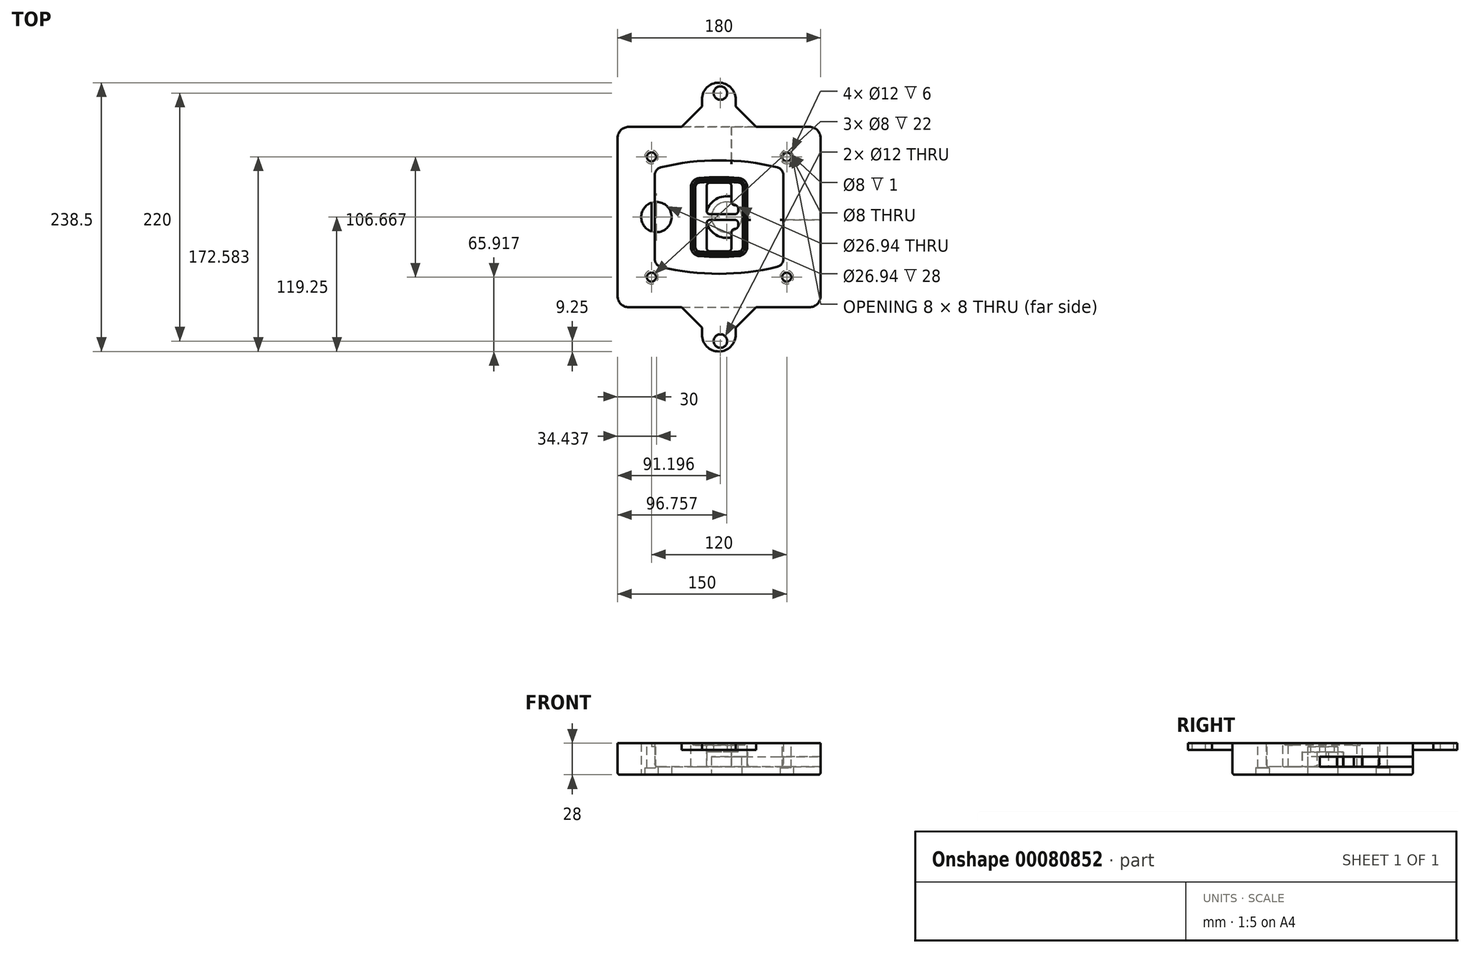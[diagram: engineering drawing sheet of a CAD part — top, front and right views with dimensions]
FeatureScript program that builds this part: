
annotation { "Feature Type Name" : "Feature", "Feature Type Description" : "" }
export const myFeature = defineFeature(function(context is Context, id is Id, definition is map)
    precondition{}
    {
        {
            var Q0;
            Q0=qCreatedBy(makeId("Top.planeOp"),FACE);
            var sketch = newSketch(context, id + "F0", { "sketchPlane" : qUnion([Q0])});
            skPoint(sketch, "E0.rect.middle", {"position": v(0, 0) * mm});
            skLineSegment(sketch, "E1.bottom", {"start": v(-80, -80) * mm, "end": v(80, -80) * mm});
            skLineSegment(sketch, "E1.top", {"start": v(-80, 80) * mm, "end": v(80, 80) * mm});
            skLineSegment(sketch, "E1.left", {"start": v(-90, -70) * mm, "end": v(-90, 70) * mm});
            skLineSegment(sketch, "E1.right", {"start": v(90, -70) * mm, "end": v(90, 70) * mm});
            skLineSegment(sketch, "E2", {"start": v(-90, 80) * mm, "end": v(90, -80) * mm, "construction": true});
            skLineSegment(sketch, "E3", {"start": v(90, 80) * mm, "end": v(-90, -80) * mm, "construction": true});
            skCircle(sketch, "E4", {"center": v(-60, 53.33) * mm, "radius": 4 * mm});
            skCircle(sketch, "E5", {"center": v(60, 53.33) * mm, "radius": 4 * mm});
            skCircle(sketch, "E6", {"center": v(60, -53.33) * mm, "radius": 4 * mm});
            skCircle(sketch, "E7", {"center": v(-60, -53.33) * mm, "radius": 4 * mm});
            skLineSegment(sketch, "E8", {"start": v(-60, 53.33) * mm, "end": v(60, 53.33) * mm, "construction": true});
            skLineSegment(sketch, "E9", {"start": v(60, 53.33) * mm, "end": v(60, -53.33) * mm, "construction": true});
            skLineSegment(sketch, "E10", {"start": v(60, -53.33) * mm, "end": v(-60, -53.33) * mm, "construction": true});
            skLineSegment(sketch, "E11", {"start": v(-60, -53.33) * mm, "end": v(-60, 53.33) * mm, "construction": true});
            skLineSegment(sketch, "E12", {"start": v(-60, 37.3) * mm, "end": v(-60, -37.3) * mm});
            skLineSegment(sketch, "E13", {"start": v(60, 37.3) * mm, "end": v(60, -37.3) * mm});
            skArc(sketch, "E14", {"start": v(52.38, 47.01) * mm, "mid": v(0, 53.33) * mm, "end": v(-52.38, 47.01) * mm});
            skArc(sketch, "E15", {"start": v(-52.38, -47.01) * mm, "mid": v(0, -53.33) * mm, "end": v(52.38, -47.01) * mm});
            skLineSegment(sketch, "E16", {"start": v(-60, 0) * mm, "end": v(60, 0) * mm, "construction": true});
            skPoint(sketch, "E17.visualSharp", {"position": v(-60, -45) * mm});
            skArc(sketch, "E17.filletArc", {"start": v(-60, -37.3) * mm, "mid": v(-57.87, -43.47) * mm, "end": v(-52.38, -47.01) * mm});
            skPoint(sketch, "E18.visualSharp", {"position": v(-60, 45) * mm});
            skArc(sketch, "E18.filletArc", {"start": v(-52.38, 47.01) * mm, "mid": v(-57.87, 43.47) * mm, "end": v(-60, 37.3) * mm});
            skPoint(sketch, "E19.visualSharp", {"position": v(60, 45) * mm});
            skArc(sketch, "E19.filletArc", {"start": v(60, 37.3) * mm, "mid": v(57.87, 43.47) * mm, "end": v(52.38, 47.01) * mm});
            skPoint(sketch, "E20.visualSharp", {"position": v(60, -45) * mm});
            skArc(sketch, "E20.filletArc", {"start": v(52.38, -47.01) * mm, "mid": v(57.87, -43.47) * mm, "end": v(60, -37.3) * mm});
            skPoint(sketch, "E21.visualSharp", {"position": v(-90, 80) * mm});
            skArc(sketch, "E21.filletArc", {"start": v(-80, 80) * mm, "mid": v(-87.07, 77.07) * mm, "end": v(-90, 70) * mm});
            skPoint(sketch, "E22.visualSharp", {"position": v(90, 80) * mm});
            skArc(sketch, "E22.filletArc", {"start": v(90, 70) * mm, "mid": v(87.07, 77.07) * mm, "end": v(80, 80) * mm});
            skPoint(sketch, "E23.visualSharp", {"position": v(90, -80) * mm});
            skArc(sketch, "E23.filletArc", {"start": v(80, -80) * mm, "mid": v(87.07, -77.07) * mm, "end": v(90, -70) * mm});
            skPoint(sketch, "E24.visualSharp", {"position": v(-90, -80) * mm});
            skArc(sketch, "E24.filletArc", {"start": v(-90, -70) * mm, "mid": v(-87.07, -77.07) * mm, "end": v(-80, -80) * mm});
            skArc(sketch, "E25.0", {"start": v(57, 37.3) * mm, "mid": v(55.5, 41.62) * mm, "end": v(51.67, 44.1) * mm});
            skLineSegment(sketch, "E25.1", {"start": v(57, 37.3) * mm, "end": v(57, -37.3) * mm});
            skArc(sketch, "E25.2", {"start": v(51.67, -44.1) * mm, "mid": v(55.5, -41.62) * mm, "end": v(57, -37.3) * mm});
            skArc(sketch, "E25.3", {"start": v(-51.67, -44.1) * mm, "mid": v(0, -50.33) * mm, "end": v(51.67, -44.1) * mm});
            skArc(sketch, "E25.4", {"start": v(-57, -37.3) * mm, "mid": v(-55.5, -41.62) * mm, "end": v(-51.67, -44.1) * mm});
            skArc(sketch, "E25.5", {"start": v(51.67, 44.1) * mm, "mid": v(0, 50.33) * mm, "end": v(-51.67, 44.1) * mm});
            skLineSegment(sketch, "E25.6", {"start": v(-57, 37.3) * mm, "end": v(-57, -37.3) * mm});
            skArc(sketch, "E25.7", {"start": v(-51.67, 44.1) * mm, "mid": v(-55.5, 41.62) * mm, "end": v(-57, 37.3) * mm});
            skArc(sketch, "E26.0", {"start": v(-53.33, 50.9) * mm, "mid": v(-61.01, 45.94) * mm, "end": v(-64, 37.3) * mm});
            skArc(sketch, "E26.1", {"start": v(53.33, 50.9) * mm, "mid": v(0, 57.33) * mm, "end": v(-53.33, 50.9) * mm});
            skArc(sketch, "E26.2", {"start": v(64, 37.3) * mm, "mid": v(61.01, 45.94) * mm, "end": v(53.33, 50.9) * mm});
            skLineSegment(sketch, "E26.3", {"start": v(64, 37.3) * mm, "end": v(64, -37.3) * mm});
            skArc(sketch, "E26.4", {"start": v(53.33, -50.9) * mm, "mid": v(61.01, -45.94) * mm, "end": v(64, -37.3) * mm});
            skLineSegment(sketch, "E26.5", {"start": v(-64, 37.3) * mm, "end": v(-64, -37.3) * mm});
            skArc(sketch, "E26.6", {"start": v(-53.33, -50.9) * mm, "mid": v(0, -57.33) * mm, "end": v(53.33, -50.9) * mm});
            skArc(sketch, "E26.7", {"start": v(-64, -37.3) * mm, "mid": v(-61.01, -45.94) * mm, "end": v(-53.33, -50.9) * mm});
            skSolve(sketch);
        }
        {
            var Q0;
            Q0=makeQuery(id+"F0.imprint","IMPRINT",FACE,{"disambiguationData":[TD([[makeQuery(id+"F0.imprint","IMPRINT",EDGE,{"derivedFrom":sQuery(id+"F0.wireOp",EDGE,"E1.bottom")}),1.0]])]});
            var Q1;
            Q1=makeQuery(id+"F0.imprint","IMPRINT",FACE,{"disambiguationData":[TD([[makeQuery(id+"F0.imprint","IMPRINT",EDGE,{"derivedFrom":sQuery(id+"F0.wireOp",EDGE,"E12")}),1.0]])]});
            var Q2;
            Q2=makeQuery(id+"F0.imprint","IMPRINT",FACE,{"disambiguationData":[TD([[makeQuery(id+"F0.imprint","IMPRINT",EDGE,{"derivedFrom":sQuery(id+"F0.wireOp",EDGE,"E25.0")}),1.0]])]});
            var Q3;
            Q3=makeQuery(id+"F0.imprint","IMPRINT",FACE,{"disambiguationData":[TD([[makeQuery(id+"F0.imprint","IMPRINT",EDGE,{"derivedFrom":sQuery(id+"F0.wireOp",EDGE,"E12")}),-1.0]])]});
            extrude(context, id + "F1", {"entities" : qUnion([Q0, Q1, Q2, Q3]), "oppositeDirection" : true, "depth" : 25 * mm});
        }
        {
            var Q0;
            Q0=makeQuery(id+"F0.imprint","IMPRINT",FACE,{"disambiguationData":[TD([[makeQuery(id+"F0.imprint","IMPRINT",EDGE,{"derivedFrom":sQuery(id+"F0.wireOp",EDGE,"E12")}),1.0]])]});
            extrude(context, id + "F2", {"entities" : qUnion([Q0]), "operationType" : NewBodyOperationType.ADD, "depth" : 3 * mm});
        }
        {
            var Q0;
            Q0=makeQuery(id+"F0.imprint","IMPRINT",FACE,{"disambiguationData":[TD([[makeQuery(id+"F0.imprint","IMPRINT",EDGE,{"derivedFrom":sQuery(id+"F0.wireOp",EDGE,"E25.0")}),1.0]])]});
            extrude(context, id + "F3", {"entities" : qUnion([Q0]), "operationType" : NewBodyOperationType.REMOVE, "oppositeDirection" : true, "depth" : 18 * mm});
        }
        {
            var Q0;
            Q0=makeQuery(id+"F2.opExtrude","CAP_FACE",FACE,{"disambiguationData":[OSD([sQuery(id+"F0.wireOp",EDGE,"E12"),sQuery(id+"F0.wireOp",EDGE,"E13"),sQuery(id+"F0.wireOp",EDGE,"E14"),sQuery(id+"F0.wireOp",EDGE,"E15"),sQuery(id+"F0.wireOp",EDGE,"E17.filletArc"),sQuery(id+"F0.wireOp",EDGE,"E18.filletArc"),sQuery(id+"F0.wireOp",EDGE,"E19.filletArc"),sQuery(id+"F0.wireOp",EDGE,"E20.filletArc"),sQuery(id+"F0.wireOp",EDGE,"E25.0"),sQuery(id+"F0.wireOp",EDGE,"E25.1"),sQuery(id+"F0.wireOp",EDGE,"E25.2"),sQuery(id+"F0.wireOp",EDGE,"E25.3"),sQuery(id+"F0.wireOp",EDGE,"E25.4"),sQuery(id+"F0.wireOp",EDGE,"E25.5"),sQuery(id+"F0.wireOp",EDGE,"E25.6"),sQuery(id+"F0.wireOp",EDGE,"E25.7")])],"isStart":false});
            var sketch = newSketch(context, id + "F4", { "sketchPlane" : qUnion([Q0])});
            skArc(sketch, "E27.0", {"start": v(-17.7, -34.56) * mm, "mid": v(0, -35.33) * mm, "end": v(17.7, -34.56) * mm});
            skArc(sketch, "E28.0", {"start": v(17.7, 34.56) * mm, "mid": v(0, 35.33) * mm, "end": v(-17.7, 34.56) * mm});
            skLineSegment(sketch, "E29", {"start": v(-25, 26.59) * mm, "end": v(-25, -26.59) * mm});
            skLineSegment(sketch, "E30", {"start": v(25, 26.59) * mm, "end": v(25, -26.59) * mm});
            skLineSegment(sketch, "E31", {"start": v(-25, 33.78) * mm, "end": v(25, 33.78) * mm, "construction": true});
            skLineSegment(sketch, "E32", {"start": v(-25, -33.78) * mm, "end": v(25, -33.78) * mm, "construction": true});
            skPoint(sketch, "E33.visualSharp", {"position": v(-25, 33.78) * mm});
            skArc(sketch, "E33.filletArc", {"start": v(-17.7, 34.56) * mm, "mid": v(-22.9, 32) * mm, "end": v(-25, 26.59) * mm});
            skPoint(sketch, "E34.visualSharp", {"position": v(25, 33.78) * mm});
            skArc(sketch, "E34.filletArc", {"start": v(25, 26.59) * mm, "mid": v(22.9, 32) * mm, "end": v(17.7, 34.56) * mm});
            skPoint(sketch, "E35.visualSharp", {"position": v(25, -33.78) * mm});
            skArc(sketch, "E35.filletArc", {"start": v(17.7, -34.56) * mm, "mid": v(22.9, -32) * mm, "end": v(25, -26.59) * mm});
            skPoint(sketch, "E36.visualSharp", {"position": v(-25, -33.78) * mm});
            skArc(sketch, "E36.filletArc", {"start": v(-25, -26.59) * mm, "mid": v(-22.9, -32) * mm, "end": v(-17.7, -34.56) * mm});
            skArc(sketch, "E37.0", {"start": v(51.67, 44.1) * mm, "mid": v(0, 50.33) * mm, "end": v(-51.67, 44.1) * mm});
            skArc(sketch, "E37.1", {"start": v(-51.67, 44.1) * mm, "mid": v(-55.5, 41.62) * mm, "end": v(-57, 37.3) * mm});
            skLineSegment(sketch, "E37.2", {"start": v(-57, 37.3) * mm, "end": v(-57, -37.3) * mm});
            skArc(sketch, "E37.3", {"start": v(-57, -37.3) * mm, "mid": v(-55.5, -41.62) * mm, "end": v(-51.67, -44.1) * mm});
            skArc(sketch, "E37.4", {"start": v(-51.67, -44.1) * mm, "mid": v(0, -50.33) * mm, "end": v(51.67, -44.1) * mm});
            skArc(sketch, "E37.5", {"start": v(51.67, -44.1) * mm, "mid": v(55.5, -41.62) * mm, "end": v(57, -37.3) * mm});
            skLineSegment(sketch, "E37.6", {"start": v(57, 37.3) * mm, "end": v(57, -37.3) * mm});
            skArc(sketch, "E37.7", {"start": v(57, 37.3) * mm, "mid": v(55.5, 41.62) * mm, "end": v(51.67, 44.1) * mm});
            skLineSegment(sketch, "E38.0", {"start": v(23, 26.59) * mm, "end": v(23, -26.59) * mm});
            skArc(sketch, "E38.1", {"start": v(17.53, -32.56) * mm, "mid": v(21.42, -30.64) * mm, "end": v(23, -26.59) * mm});
            skArc(sketch, "E38.2", {"start": v(-17.53, -32.56) * mm, "mid": v(0, -33.33) * mm, "end": v(17.53, -32.56) * mm});
            skArc(sketch, "E38.3", {"start": v(-23, -26.59) * mm, "mid": v(-21.42, -30.64) * mm, "end": v(-17.53, -32.56) * mm});
            skLineSegment(sketch, "E38.4", {"start": v(-23, 26.59) * mm, "end": v(-23, -26.59) * mm});
            skArc(sketch, "E38.5", {"start": v(23, 26.59) * mm, "mid": v(21.42, 30.64) * mm, "end": v(17.53, 32.56) * mm});
            skArc(sketch, "E38.6", {"start": v(-17.53, 32.56) * mm, "mid": v(-21.42, 30.64) * mm, "end": v(-23, 26.59) * mm});
            skArc(sketch, "E38.7", {"start": v(17.53, 32.56) * mm, "mid": v(0, 33.33) * mm, "end": v(-17.53, 32.56) * mm});
            skArc(sketch, "E39.0", {"start": v(21, 26.59) * mm, "mid": v(19.95, 29.29) * mm, "end": v(17.35, 30.57) * mm});
            skLineSegment(sketch, "E39.1", {"start": v(21, 26.59) * mm, "end": v(21, -26.59) * mm});
            skArc(sketch, "E39.2", {"start": v(17.35, -30.57) * mm, "mid": v(19.95, -29.29) * mm, "end": v(21, -26.59) * mm});
            skArc(sketch, "E39.3", {"start": v(-17.35, -30.57) * mm, "mid": v(0, -31.33) * mm, "end": v(17.35, -30.57) * mm});
            skArc(sketch, "E39.4", {"start": v(-21, -26.59) * mm, "mid": v(-19.95, -29.29) * mm, "end": v(-17.35, -30.57) * mm});
            skArc(sketch, "E39.5", {"start": v(17.35, 30.57) * mm, "mid": v(0, 31.33) * mm, "end": v(-17.35, 30.57) * mm});
            skLineSegment(sketch, "E39.6", {"start": v(-21, 26.59) * mm, "end": v(-21, -26.59) * mm});
            skArc(sketch, "E39.7", {"start": v(-17.35, 30.57) * mm, "mid": v(-19.95, 29.29) * mm, "end": v(-21, 26.59) * mm});
            skLineSegment(sketch, "E40", {"start": v(-25, 0) * mm, "end": v(25, 0) * mm, "construction": true});
            skLineSegment(sketch, "E41", {"start": v(-11, 5.5) * mm, "end": v(-11, 27.5) * mm});
            skLineSegment(sketch, "E42", {"start": v(-8, 30.5) * mm, "end": v(8, 30.5) * mm});
            skLineSegment(sketch, "E43", {"start": v(11, 27.5) * mm, "end": v(11, 13.5) * mm});
            skLineSegment(sketch, "E44", {"start": v(14, 10.5) * mm, "end": v(14, 10.5) * mm});
            skLineSegment(sketch, "E45", {"start": v(17, 7.5) * mm, "end": v(17, 5.5) * mm});
            skLineSegment(sketch, "E46", {"start": v(14, 2.5) * mm, "end": v(-8, 2.5) * mm});
            skPoint(sketch, "E47.visualSharp", {"position": v(-11, 30.5) * mm});
            skArc(sketch, "E47.filletArc", {"start": v(-8, 30.5) * mm, "mid": v(-10.12, 29.62) * mm, "end": v(-11, 27.5) * mm});
            skPoint(sketch, "E48.visualSharp", {"position": v(11, 30.5) * mm});
            skArc(sketch, "E48.filletArc", {"start": v(11, 27.5) * mm, "mid": v(10.12, 29.62) * mm, "end": v(8, 30.5) * mm});
            skPoint(sketch, "E49.visualSharp", {"position": v(11, 10.5) * mm});
            skArc(sketch, "E49.filletArc", {"start": v(11, 13.5) * mm, "mid": v(11.88, 11.38) * mm, "end": v(14, 10.5) * mm});
            skPoint(sketch, "E50.visualSharp", {"position": v(17, 10.5) * mm});
            skArc(sketch, "E50.filletArc", {"start": v(17, 7.5) * mm, "mid": v(16.12, 9.62) * mm, "end": v(14, 10.5) * mm});
            skPoint(sketch, "E51.visualSharp", {"position": v(17, 2.5) * mm});
            skArc(sketch, "E51.filletArc", {"start": v(14, 2.5) * mm, "mid": v(16.12, 3.38) * mm, "end": v(17, 5.5) * mm});
            skPoint(sketch, "E52.visualSharp", {"position": v(-11, 2.5) * mm});
            skArc(sketch, "E52.filletArc", {"start": v(-11, 5.5) * mm, "mid": v(-10.12, 3.38) * mm, "end": v(-8, 2.5) * mm});
            skLineSegment(sketch, "E53.0.MirrorCS", {"start": v(14, -2.5) * mm, "end": v(-8, -2.5) * mm});
            skArc(sketch, "E54.0.MirrorCS", {"start": v(-11, -5.5) * mm, "mid": v(-10.12, -3.38) * mm, "end": v(-8, -2.5) * mm});
            skLineSegment(sketch, "E55.0.MirrorCS", {"start": v(-11, -5.5) * mm, "end": v(-11, -27.5) * mm});
            skArc(sketch, "E56.0.MirrorCS", {"start": v(-8, -30.5) * mm, "mid": v(-10.12, -29.62) * mm, "end": v(-11, -27.5) * mm});
            skLineSegment(sketch, "E57.0.MirrorCS", {"start": v(-8, -30.5) * mm, "end": v(8, -30.5) * mm});
            skArc(sketch, "E58.0.MirrorCS", {"start": v(11, -27.5) * mm, "mid": v(10.12, -29.62) * mm, "end": v(8, -30.5) * mm});
            skLineSegment(sketch, "E59.0.MirrorCS", {"start": v(11, -27.5) * mm, "end": v(11, -13.5) * mm});
            skArc(sketch, "E60.0.MirrorCS", {"start": v(11, -13.5) * mm, "mid": v(11.88, -11.38) * mm, "end": v(14, -10.5) * mm});
            skArc(sketch, "E61.0.MirrorCS", {"start": v(17, -7.5) * mm, "mid": v(16.12, -9.62) * mm, "end": v(14, -10.5) * mm});
            skLineSegment(sketch, "E62.0.MirrorCS", {"start": v(17, -7.5) * mm, "end": v(17, -5.5) * mm});
            skArc(sketch, "E63.0.MirrorCS", {"start": v(14, -2.5) * mm, "mid": v(16.12, -3.38) * mm, "end": v(17, -5.5) * mm});
            skSolve(sketch);
        }
        {
            var Q0;
            Q0=makeQuery(id+"F4.imprint","IMPRINT",FACE,{"disambiguationData":[TD([[makeQuery(id+"F4.imprint","IMPRINT",EDGE,{"derivedFrom":sQuery(id+"F4.wireOp",EDGE,"E27.0")}),1.0]])]});
            var Q1;
            Q1=makeQuery(id+"F4.imprint","IMPRINT",FACE,{"disambiguationData":[TD([[makeQuery(id+"F4.imprint","IMPRINT",EDGE,{"derivedFrom":sQuery(id+"F4.wireOp",EDGE,"E38.0")}),-1.0]])]});
            var Q2;
            Q2=makeQuery(id+"F4.imprint","IMPRINT",FACE,{"disambiguationData":[TD([[makeQuery(id+"F4.imprint","IMPRINT",EDGE,{"derivedFrom":sQuery(id+"F4.wireOp",EDGE,"E39.0")}),1.0]])]});
            extrude(context, id + "F5", {"entities" : qUnion([Q0, Q1, Q2]), "operationType" : NewBodyOperationType.ADD, "endBound" : BoundingType.UP_TO_NEXT, "oppositeDirection" : true, "depth" : 25 * mm});
        }
        {
            var Q0;
            Q0=makeQuery(id+"F4.imprint","IMPRINT",FACE,{"disambiguationData":[TD([[makeQuery(id+"F4.imprint","IMPRINT",EDGE,{"derivedFrom":sQuery(id+"F4.wireOp",EDGE,"E38.0")}),-1.0]])]});
            extrude(context, id + "F6", {"entities" : qUnion([Q0]), "operationType" : NewBodyOperationType.REMOVE, "oppositeDirection" : true, "depth" : 2 * mm});
        }
        {
            var Q0;
            Q0=makeQuery(id+"F1.opExtrude","CAP_FACE",FACE,{"disambiguationData":[OSD([sQuery(id+"F0.wireOp",EDGE,"E1.bottom"),sQuery(id+"F0.wireOp",EDGE,"E1.top"),sQuery(id+"F0.wireOp",EDGE,"E1.left"),sQuery(id+"F0.wireOp",EDGE,"E1.right"),sQuery(id+"F0.wireOp",EDGE,"E4"),sQuery(id+"F0.wireOp",EDGE,"E5"),sQuery(id+"F0.wireOp",EDGE,"E6"),sQuery(id+"F0.wireOp",EDGE,"E7"),sQuery(id+"F0.wireOp",EDGE,"E21.filletArc"),sQuery(id+"F0.wireOp",EDGE,"E22.filletArc"),sQuery(id+"F0.wireOp",EDGE,"E23.filletArc"),sQuery(id+"F0.wireOp",EDGE,"E24.filletArc")])],"isStart":false});
            var sketch = newSketch(context, id + "F7", { "sketchPlane" : qUnion([Q0])});
            skCircle(sketch, "E64", {"center": v(6.76, 0) * mm, "radius": 13.47 * mm});
            skCircle(sketch, "E65", {"center": v(-55.56, 0) * mm, "radius": 13.47 * mm});
            skLineSegment(sketch, "E66", {"start": v(90, 0) * mm, "end": v(-90, 0) * mm});
            skCircle(sketch, "E67", {"center": v(6.76, 0) * mm, "radius": 18.47 * mm});
            skCircle(sketch, "E68", {"center": v(60, -53.33) * mm, "radius": 6 * mm});
            skCircle(sketch, "E69", {"center": v(-60, -53.33) * mm, "radius": 6 * mm});
            skCircle(sketch, "E70", {"center": v(-60, 53.33) * mm, "radius": 6 * mm});
            skCircle(sketch, "E71", {"center": v(60, 53.33) * mm, "radius": 6 * mm});
            skSolve(sketch);
        }
        {
            var Q0;
            {var subQ1=sQuery(id+"F7.wireOp",EDGE,"E66");var subQ4=sQuery(id+"F7.wireOp",EDGE,"E64");var subQ6=makeQuery(id+"F7.imprint","INTERSECT",VERTEX,{"disambiguationData":[OD(0.0)],"derivedFrom":[subQ4,subQ1]});Q0=makeQuery(id+"F7.imprint","IMPRINT",FACE,{"disambiguationData":[TD([[makeQuery(id+"F7.imprint","IMPRINT",EDGE,{"disambiguationData":[TD([[subQ6,-1.0]])],"derivedFrom":subQ4}),-1.0]])]});}
            var Q1;
            {var subQ0=sQuery(id+"F7.wireOp",EDGE,"E66");var subQ1=sQuery(id+"F7.wireOp",EDGE,"E64");var subQ3=makeQuery(id+"F7.imprint","INTERSECT",VERTEX,{"disambiguationData":[OD(0.0)],"derivedFrom":[subQ1,subQ0]});Q1=makeQuery(id+"F7.imprint","IMPRINT",FACE,{"disambiguationData":[TD([[makeQuery(id+"F7.imprint","IMPRINT",EDGE,{"disambiguationData":[TD([[subQ3,-1.0]])],"derivedFrom":subQ1}),1.0]])]});}
            var Q2;
            {var subQ0=sQuery(id+"F7.wireOp",EDGE,"E66");var subQ1=sQuery(id+"F7.wireOp",EDGE,"E64");var subQ3=makeQuery(id+"F7.imprint","INTERSECT",VERTEX,{"disambiguationData":[OD(0.0)],"derivedFrom":[subQ1,subQ0]});Q2=makeQuery(id+"F7.imprint","IMPRINT",FACE,{"disambiguationData":[TD([[makeQuery(id+"F7.imprint","IMPRINT",EDGE,{"disambiguationData":[TD([[subQ3,1.0]])],"derivedFrom":subQ1}),1.0]])]});}
            var Q3;
            {var subQ1=sQuery(id+"F7.wireOp",EDGE,"E66");var subQ4=sQuery(id+"F7.wireOp",EDGE,"E64");var subQ6=makeQuery(id+"F7.imprint","INTERSECT",VERTEX,{"disambiguationData":[OD(0.0)],"derivedFrom":[subQ4,subQ1]});Q3=makeQuery(id+"F7.imprint","IMPRINT",FACE,{"disambiguationData":[TD([[makeQuery(id+"F7.imprint","IMPRINT",EDGE,{"disambiguationData":[TD([[subQ6,1.0]])],"derivedFrom":subQ4}),-1.0]])]});}
            extrude(context, id + "F8", {"entities" : qUnion([Q0, Q1, Q2, Q3]), "operationType" : NewBodyOperationType.ADD, "oppositeDirection" : true, "depth" : 20 * mm});
        }
        {
            var Q0;
            {var subQ0=sQuery(id+"F7.wireOp",EDGE,"E66");var subQ1=sQuery(id+"F7.wireOp",EDGE,"E64");var subQ3=makeQuery(id+"F7.imprint","INTERSECT",VERTEX,{"disambiguationData":[OD(0.0)],"derivedFrom":[subQ1,subQ0]});Q0=makeQuery(id+"F7.imprint","IMPRINT",FACE,{"disambiguationData":[TD([[makeQuery(id+"F7.imprint","IMPRINT",EDGE,{"disambiguationData":[TD([[subQ3,-1.0]])],"derivedFrom":subQ1}),1.0]])]});}
            var Q1;
            {var subQ0=sQuery(id+"F7.wireOp",EDGE,"E66");var subQ1=sQuery(id+"F7.wireOp",EDGE,"E64");var subQ3=makeQuery(id+"F7.imprint","INTERSECT",VERTEX,{"disambiguationData":[OD(0.0)],"derivedFrom":[subQ1,subQ0]});Q1=makeQuery(id+"F7.imprint","IMPRINT",FACE,{"disambiguationData":[TD([[makeQuery(id+"F7.imprint","IMPRINT",EDGE,{"disambiguationData":[TD([[subQ3,1.0]])],"derivedFrom":subQ1}),1.0]])]});}
            extrude(context, id + "F9", {"entities" : qUnion([Q0, Q1]), "operationType" : NewBodyOperationType.REMOVE, "oppositeDirection" : true, "depth" : 16 * mm});
        }
        {
            var Q0;
            {var subQ0=sQuery(id+"F7.wireOp",EDGE,"E66");var subQ1=sQuery(id+"F7.wireOp",EDGE,"E65");var subQ3=makeQuery(id+"F7.imprint","INTERSECT",VERTEX,{"disambiguationData":[OD(0.0)],"derivedFrom":[subQ1,subQ0]});Q0=makeQuery(id+"F7.imprint","IMPRINT",FACE,{"disambiguationData":[TD([[makeQuery(id+"F7.imprint","IMPRINT",EDGE,{"disambiguationData":[TD([[subQ3,-1.0]])],"derivedFrom":subQ1}),1.0]])]});}
            var Q1;
            {var subQ0=sQuery(id+"F7.wireOp",EDGE,"E66");var subQ1=sQuery(id+"F7.wireOp",EDGE,"E65");var subQ3=makeQuery(id+"F7.imprint","INTERSECT",VERTEX,{"disambiguationData":[OD(0.0)],"derivedFrom":[subQ1,subQ0]});Q1=makeQuery(id+"F7.imprint","IMPRINT",FACE,{"disambiguationData":[TD([[makeQuery(id+"F7.imprint","IMPRINT",EDGE,{"disambiguationData":[TD([[subQ3,1.0]])],"derivedFrom":subQ1}),1.0]])]});}
            extrude(context, id + "F10", {"entities" : qUnion([Q0, Q1]), "operationType" : NewBodyOperationType.REMOVE, "oppositeDirection" : true, "depth" : 25 * mm});
        }
        {
            var Q0;
            Q0=makeQuery(id+"F7.imprint","IMPRINT",FACE,{"disambiguationData":[TD([[makeQuery(id+"F7.imprint","IMPRINT",EDGE,{"derivedFrom":sQuery(id+"F7.wireOp",EDGE,"E68")}),1.0]])]});
            var Q1;
            Q1=makeQuery(id+"F7.imprint","IMPRINT",FACE,{"disambiguationData":[TD([[makeQuery(id+"F7.imprint","IMPRINT",EDGE,{"derivedFrom":makeQuery(id+"F1.opExtrude","CAP_EDGE",EDGE,{"disambiguationData":[OSD([sQuery(id+"F0.wireOp",EDGE,"E5")])],"isStart":false})}),-1.0]])]});
            var Q2;
            Q2=makeQuery(id+"F7.imprint","IMPRINT",FACE,{"disambiguationData":[TD([[makeQuery(id+"F7.imprint","IMPRINT",EDGE,{"derivedFrom":sQuery(id+"F7.wireOp",EDGE,"E69")}),1.0]])]});
            var Q3;
            Q3=makeQuery(id+"F7.imprint","IMPRINT",FACE,{"disambiguationData":[TD([[makeQuery(id+"F7.imprint","IMPRINT",EDGE,{"derivedFrom":makeQuery(id+"F1.opExtrude","CAP_EDGE",EDGE,{"disambiguationData":[OSD([sQuery(id+"F0.wireOp",EDGE,"E4")])],"isStart":false})}),-1.0]])]});
            var Q4;
            Q4=makeQuery(id+"F7.imprint","IMPRINT",FACE,{"disambiguationData":[TD([[makeQuery(id+"F7.imprint","IMPRINT",EDGE,{"derivedFrom":sQuery(id+"F7.wireOp",EDGE,"E70")}),1.0]])]});
            var Q5;
            Q5=makeQuery(id+"F7.imprint","IMPRINT",FACE,{"disambiguationData":[TD([[makeQuery(id+"F7.imprint","IMPRINT",EDGE,{"derivedFrom":makeQuery(id+"F1.opExtrude","CAP_EDGE",EDGE,{"disambiguationData":[OSD([sQuery(id+"F0.wireOp",EDGE,"E7")])],"isStart":false})}),-1.0]])]});
            var Q6;
            Q6=makeQuery(id+"F7.imprint","IMPRINT",FACE,{"disambiguationData":[TD([[makeQuery(id+"F7.imprint","IMPRINT",EDGE,{"derivedFrom":sQuery(id+"F7.wireOp",EDGE,"E71")}),1.0]])]});
            var Q7;
            Q7=makeQuery(id+"F7.imprint","IMPRINT",FACE,{"disambiguationData":[TD([[makeQuery(id+"F7.imprint","IMPRINT",EDGE,{"derivedFrom":makeQuery(id+"F1.opExtrude","CAP_EDGE",EDGE,{"disambiguationData":[OSD([sQuery(id+"F0.wireOp",EDGE,"E6")])],"isStart":false})}),-1.0]])]});
            extrude(context, id + "F11", {"entities" : qUnion([Q0, Q1, Q2, Q3, Q4, Q5, Q6, Q7]), "operationType" : NewBodyOperationType.REMOVE, "oppositeDirection" : true, "depth" : 6 * mm});
        }
        {
            var Q0;
            Q0=makeQuery(id+"F9.boolean.opBoolean","COPY",FACE,{"derivedFrom":makeQuery(id+"F9.opExtrude","CAP_FACE",FACE,{"disambiguationData":[OSD([sQuery(id+"F7.wireOp",EDGE,"E64")])],"isStart":false})});
            var sketch = newSketch(context, id + "F12", { "sketchPlane" : qUnion([Q0])});
            skArc(sketch, "E72.0", {"start": v(11, -88.19) * mm, "mid": v(97.1, -83.6) * mm, "end": v(92.5, 2.5) * mm});
            skLineSegment(sketch, "E72.1", {"start": v(11, -17.97) * mm, "end": v(11, -17.97) * mm});
            skLineSegment(sketch, "E73", {"start": v(92.5, -105.13) * mm, "end": v(102.3, -105.13) * mm});
            skLineSegment(sketch, "E74.0", {"start": v(92.5, 2.5) * mm, "end": v(14, 2.5) * mm});
            skArc(sketch, "E74.1", {"start": v(14, 2.5) * mm, "mid": v(16.12, 3.38) * mm, "end": v(17, 5.5) * mm});
            skLineSegment(sketch, "E74.2", {"start": v(17, 7.5) * mm, "end": v(17, 5.5) * mm});
            skArc(sketch, "E74.3", {"start": v(17, 7.5) * mm, "mid": v(16.12, 9.62) * mm, "end": v(14, 10.5) * mm});
            skArc(sketch, "E74.4", {"start": v(11, 13.5) * mm, "mid": v(11.88, 11.38) * mm, "end": v(14, 10.5) * mm});
            skLineSegment(sketch, "E74.5", {"start": v(11, 13.5) * mm, "end": v(11, -88.19) * mm});
            skLineSegment(sketch, "E74.7", {"start": v(92.5, -2.5) * mm, "end": v(14, -2.5) * mm});
            skArc(sketch, "E74.8", {"start": v(14, -2.5) * mm, "mid": v(16.12, -3.38) * mm, "end": v(17, -5.5) * mm});
            skLineSegment(sketch, "E74.9", {"start": v(17, -7.5) * mm, "end": v(17, -5.5) * mm});
            skArc(sketch, "E74.10", {"start": v(17, -7.5) * mm, "mid": v(16.12, -9.62) * mm, "end": v(14, -10.5) * mm});
            skArc(sketch, "E74.11", {"start": v(11, -13.5) * mm, "mid": v(11.88, -11.38) * mm, "end": v(14, -10.5) * mm});
            skLineSegment(sketch, "E74.12", {"start": v(11, -17.97) * mm, "end": v(11, -13.5) * mm});
            skPoint(sketch, "E75.orphan", {"position": v(11, -27.5) * mm});
            skPoint(sketch, "E76.orphan", {"position": v(-8, -2.5) * mm});
            skPoint(sketch, "E77.orphan", {"position": v(-8, 2.5) * mm});
            skPoint(sketch, "E78.orphan", {"position": v(11, 27.5) * mm});
            skSolve(sketch);
        }
        {
            var Q0;
            {var subQ7=sQuery(id+"F12.wireOp",EDGE,"E72.0");var subQ14=sQuery(id+"F12.wireOp",EDGE,"E72.1");var subQ16=sQuery(id+"F12.wireOp",EDGE,"E74.1");var subQ18=sQuery(id+"F12.wireOp",EDGE,"E74.8");Q0=qUnion([makeQuery(id+"F12.imprint","IMPRINT",FACE,{"disambiguationData":[TD([[makeQuery(id+"F12.imprint","IMPRINT",EDGE,{"derivedFrom":subQ7}),1.0]])]}),makeQuery(id+"F12.imprint","IMPRINT",FACE,{"disambiguationData":[TD([[makeQuery(id+"F12.imprint","IMPRINT",EDGE,{"derivedFrom":subQ14}),1.0]])]}),makeQuery(id+"F12.imprint","IMPRINT",FACE,{"disambiguationData":[TD([[makeQuery(id+"F12.imprint","IMPRINT",EDGE,{"derivedFrom":subQ16}),1.0]])]}),makeQuery(id+"F12.imprint","IMPRINT",FACE,{"disambiguationData":[TD([[makeQuery(id+"F12.imprint","IMPRINT",EDGE,{"derivedFrom":subQ18}),-1.0]])]})]);}
            var Q1;
            Q1=makeQuery(id+"F5.boolean.opBoolean","SPLIT",FACE,{"disambiguationData":[TD([makeQuery(id+"F5.opExtrude","SWEPT_FACE",FACE,{"disambiguationData":[OSD([sQuery(id+"F4.wireOp",EDGE,"E41")])]})])],"derivedFrom":makeQuery(id+"F3.boolean.opBoolean","COPY",FACE,{"derivedFrom":makeQuery(id+"F3.opExtrude","CAP_FACE",FACE,{"disambiguationData":[OSD([sQuery(id+"F0.wireOp",EDGE,"E25.0"),sQuery(id+"F0.wireOp",EDGE,"E25.1"),sQuery(id+"F0.wireOp",EDGE,"E25.2"),sQuery(id+"F0.wireOp",EDGE,"E25.3"),sQuery(id+"F0.wireOp",EDGE,"E25.4"),sQuery(id+"F0.wireOp",EDGE,"E25.5"),sQuery(id+"F0.wireOp",EDGE,"E25.6"),sQuery(id+"F0.wireOp",EDGE,"E25.7")])],"isStart":false})})});
            extrude(context, id + "F13", {"entities" : qUnion([Q0]), "operationType" : NewBodyOperationType.REMOVE, "endBound" : BoundingType.UP_TO_SURFACE, "endBoundEntityFace" : qUnion([Q1]), "depth" : 25 * mm});
        }
        {
            var Q0;
            Q0=makeQuery(id+"F3.boolean.opBoolean","COPY",EDGE,{"derivedFrom":makeQuery(id+"F3.opExtrude","CAP_EDGE",EDGE,{"disambiguationData":[OSD([sQuery(id+"F0.wireOp",EDGE,"E25.6")])],"isStart":false})});
            var Q1;
            Q1=makeQuery(id+"F8.boolean.opBoolean","INTERSECT",EDGE,{"derivedFrom":[makeQuery(id+"F5.opExtrude","SWEPT_FACE",FACE,{"disambiguationData":[OSD([sQuery(id+"F4.wireOp",EDGE,"E30")])]}),makeQuery(id+"F8.opExtrude","CAP_FACE",FACE,{"disambiguationData":[OSD([sQuery(id+"F7.wireOp",EDGE,"E67")])],"isStart":false})]});
            var Q2;
            Q2=makeQuery(id+"F8.boolean.opBoolean","INTERSECT",EDGE,{"disambiguationData":[OD(1.0)],"derivedFrom":[makeQuery(id+"F5.opExtrude","SWEPT_FACE",FACE,{"disambiguationData":[OSD([sQuery(id+"F4.wireOp",EDGE,"E30")])]}),makeQuery(id+"F8.opExtrude","SWEPT_FACE",FACE,{"disambiguationData":[OSD([sQuery(id+"F7.wireOp",EDGE,"E67")])]})]});
            var Q3;
            {var subQ0=makeQuery(id+"F3.boolean.opBoolean","COPY",FACE,{"derivedFrom":makeQuery(id+"F3.opExtrude","CAP_FACE",FACE,{"disambiguationData":[OSD([sQuery(id+"F0.wireOp",EDGE,"E25.0"),sQuery(id+"F0.wireOp",EDGE,"E25.1"),sQuery(id+"F0.wireOp",EDGE,"E25.2"),sQuery(id+"F0.wireOp",EDGE,"E25.3"),sQuery(id+"F0.wireOp",EDGE,"E25.4"),sQuery(id+"F0.wireOp",EDGE,"E25.5"),sQuery(id+"F0.wireOp",EDGE,"E25.6"),sQuery(id+"F0.wireOp",EDGE,"E25.7")])],"isStart":false})});var subQ1=sQuery(id+"F4.wireOp",EDGE,"E30");Q3=makeQuery(id+"F8.boolean.opBoolean","SPLIT",EDGE,{"disambiguationData":[TD([makeQuery(id+"F5.opExtrude","SWEPT_FACE",FACE,{"disambiguationData":[OSD([sQuery(id+"F4.wireOp",EDGE,"E35.filletArc")])]})])],"derivedFrom":makeQuery(id+"F5.opExtrude","TWEAK_EDGE",EDGE,{"derivedFrom":[subQ0,makeQuery(id+"F4.imprint","IMPRINT",EDGE,{"derivedFrom":subQ1})]})});}
            var Q4;
            {var subQ0=sQuery(id+"F0.wireOp",EDGE,"E25.0");var subQ1=sQuery(id+"F0.wireOp",EDGE,"E25.1");var subQ2=sQuery(id+"F0.wireOp",EDGE,"E25.2");var subQ3=sQuery(id+"F0.wireOp",EDGE,"E25.3");var subQ4=sQuery(id+"F0.wireOp",EDGE,"E25.4");var subQ5=sQuery(id+"F0.wireOp",EDGE,"E25.5");var subQ6=sQuery(id+"F0.wireOp",EDGE,"E25.6");var subQ7=sQuery(id+"F0.wireOp",EDGE,"E25.7");Q4=makeQuery(id+"F8.boolean.opBoolean","INTERSECT",EDGE,{"derivedFrom":[makeQuery(id+"F5.boolean.opBoolean","SPLIT",FACE,{"disambiguationData":[TD([makeQuery(id+"F2.opExtrude","SWEPT_FACE",FACE,{"disambiguationData":[OSD([subQ0])]})])],"derivedFrom":makeQuery(id+"F3.boolean.opBoolean","COPY",FACE,{"derivedFrom":makeQuery(id+"F3.opExtrude","CAP_FACE",FACE,{"disambiguationData":[OSD([subQ0,subQ1,subQ2,subQ3,subQ4,subQ5,subQ6,subQ7])],"isStart":false})})}),makeQuery(id+"F8.opExtrude","SWEPT_FACE",FACE,{"disambiguationData":[OSD([sQuery(id+"F7.wireOp",EDGE,"E67")])]})]});}
            var Q5;
            Q5=makeQuery(id+"F8.boolean.opBoolean","INTERSECT",EDGE,{"disambiguationData":[OD(0.0)],"derivedFrom":[makeQuery(id+"F5.opExtrude","SWEPT_FACE",FACE,{"disambiguationData":[OSD([sQuery(id+"F4.wireOp",EDGE,"E30")])]}),makeQuery(id+"F8.opExtrude","SWEPT_FACE",FACE,{"disambiguationData":[OSD([sQuery(id+"F7.wireOp",EDGE,"E67")])]})]});
            fillet(context, id + "F14", {"entities" : qUnion([Q0, Q1, Q2, Q3, Q4, Q5]), "radius" : 3 * mm, "tangentPropagation" : true, "allowEdgeOverflow" : false});
        }
        {
            var Q0;
            Q0=makeQuery(id+"F1.opExtrude","CAP_EDGE",EDGE,{"disambiguationData":[OSD([sQuery(id+"F0.wireOp",EDGE,"E1.bottom")])],"isStart":false});
            fillet(context, id + "F15", {"entities" : qUnion([Q0]), "radius" : 2 * mm, "tangentPropagation" : true, "allowEdgeOverflow" : false});
        }
        {
            var Q0;
            {var subQ0=sQuery(id+"F0.wireOp",EDGE,"E22.filletArc");var subQ1=sQuery(id+"F0.wireOp",EDGE,"E7");var subQ2=sQuery(id+"F0.wireOp",EDGE,"E6");var subQ3=sQuery(id+"F0.wireOp",EDGE,"E5");var subQ4=sQuery(id+"F0.wireOp",EDGE,"E4");var subQ5=sQuery(id+"F0.wireOp",EDGE,"E1.bottom");var subQ6=sQuery(id+"F0.wireOp",EDGE,"E21.filletArc");var subQ7=sQuery(id+"F0.wireOp",EDGE,"E1.top");var subQ8=sQuery(id+"F0.wireOp",EDGE,"E1.left");var subQ9=sQuery(id+"F0.wireOp",EDGE,"E1.right");var subQ10=sQuery(id+"F0.wireOp",EDGE,"E23.filletArc");var subQ11=sQuery(id+"F0.wireOp",EDGE,"E24.filletArc");Q0=makeQuery(id+"F2.boolean.opBoolean","SPLIT",FACE,{"disambiguationData":[TD([makeQuery(id+"F1.opExtrude","SWEPT_FACE",FACE,{"disambiguationData":[OSD([subQ5])]})])],"derivedFrom":makeQuery(id+"F1.opExtrude","CAP_FACE",FACE,{"disambiguationData":[OSD([subQ5,subQ7,subQ8,subQ9,subQ4,subQ3,subQ2,subQ1,subQ6,subQ0,subQ10,subQ11])],"isStart":true})});}
            var sketch = newSketch(context, id + "F16", { "sketchPlane" : qUnion([Q0])});
            skArc(sketch, "E79.0", {"start": v(-80, 80) * mm, "mid": v(-87.07, 77.07) * mm, "end": v(-90, 70) * mm});
            skLineSegment(sketch, "E79.1", {"start": v(-80, 80) * mm, "end": v(80, 80) * mm});
            skCircle(sketch, "E79.2", {"center": v(-60, 53.33) * mm, "radius": 4 * mm});
            skArc(sketch, "E79.3", {"start": v(90, 70) * mm, "mid": v(87.07, 77.07) * mm, "end": v(80, 80) * mm});
            skCircle(sketch, "E79.4", {"center": v(60, 53.33) * mm, "radius": 4 * mm});
            skLineSegment(sketch, "E79.5", {"start": v(90, -70) * mm, "end": v(90, 70) * mm});
            skLineSegment(sketch, "E79.6", {"start": v(-90, -70) * mm, "end": v(-90, 70) * mm});
            skCircle(sketch, "E79.7", {"center": v(-60, -53.33) * mm, "radius": 4 * mm});
            skArc(sketch, "E79.8", {"start": v(-90, -70) * mm, "mid": v(-87.07, -77.07) * mm, "end": v(-80, -80) * mm});
            skArc(sketch, "E79.9", {"start": v(80, -80) * mm, "mid": v(87.07, -77.07) * mm, "end": v(90, -70) * mm});
            skCircle(sketch, "E79.10", {"center": v(60, -53.33) * mm, "radius": 4 * mm});
            skLineSegment(sketch, "E79.11", {"start": v(-80, -80) * mm, "end": v(80, -80) * mm});
            skCircle(sketch, "E80", {"center": v(1.2, 110) * mm, "radius": 6 * mm});
            skLineSegment(sketch, "E81", {"start": v(-33.22, 80) * mm, "end": v(-15.22, 98) * mm});
            skLineSegment(sketch, "E82", {"start": v(-15.22, 98) * mm, "end": v(-15.22, 104.25) * mm});
            skLineSegment(sketch, "E83", {"start": v(32.78, 80) * mm, "end": v(14.78, 98) * mm});
            skLineSegment(sketch, "E84", {"start": v(14.78, 98) * mm, "end": v(14.78, 104.25) * mm});
            skArc(sketch, "E85", {"start": v(14.78, 104.25) * mm, "mid": v(-0.22, 119.25) * mm, "end": v(-15.22, 104.25) * mm});
            skLineSegment(sketch, "E86", {"start": v(1.2, 110) * mm, "end": v(0, 80) * mm, "construction": true});
            skLineSegment(sketch, "E87", {"start": v(-90, 0) * mm, "end": v(90, 0) * mm, "construction": true});
            skLineSegment(sketch, "E88.MirrorCS", {"start": v(32.78, -80) * mm, "end": v(14.78, -98) * mm});
            skLineSegment(sketch, "E89.MirrorCS", {"start": v(14.78, -98) * mm, "end": v(14.78, -104.25) * mm});
            skArc(sketch, "E90.MirrorCS", {"start": v(14.78, -104.25) * mm, "mid": v(-0.22, -119.25) * mm, "end": v(-15.22, -104.25) * mm});
            skLineSegment(sketch, "E91.MirrorCS", {"start": v(-15.22, -98) * mm, "end": v(-15.22, -104.25) * mm});
            skLineSegment(sketch, "E92.MirrorCS", {"start": v(-33.22, -80) * mm, "end": v(-15.22, -98) * mm});
            skCircle(sketch, "E93.MirrorC", {"center": v(1.2, -110) * mm, "radius": 6 * mm});
            skLineSegment(sketch, "E94.MirrorCS", {"start": v(1.2, -110) * mm, "end": v(0, -80) * mm, "construction": true});
            skSolve(sketch);
        }
        {
            var Q0;
            Q0=makeQuery(id+"F16.imprint","IMPRINT",FACE,{"disambiguationData":[TD([[makeQuery(id+"F16.imprint","IMPRINT",EDGE,{"derivedFrom":sQuery(id+"F16.wireOp",EDGE,"E80")}),-1.0]])]});
            var Q1;
            {var subQ9=sQuery(id+"F16.wireOp",EDGE,"E79.0");Q1=makeQuery(id+"F16.imprint","IMPRINT",FACE,{"disambiguationData":[TD([[makeQuery(id+"F16.imprint","IMPRINT",EDGE,{"derivedFrom":subQ9}),1.0]])]});}
            var Q2;
            {var subQ0=sQuery(id+"F16.wireOp",EDGE,"E88.MirrorCS");Q2=makeQuery(id+"F16.imprint","IMPRINT",FACE,{"disambiguationData":[TD([[makeQuery(id+"F16.imprint","IMPRINT",EDGE,{"derivedFrom":subQ0}),-1.0]])]});}
            extrude(context, id + "F17", {"entities" : qUnion([Q0, Q1, Q2]), "operationType" : NewBodyOperationType.ADD, "endBound" : BoundingType.SYMMETRIC, "depth" : 6 * mm});
        }
    });
